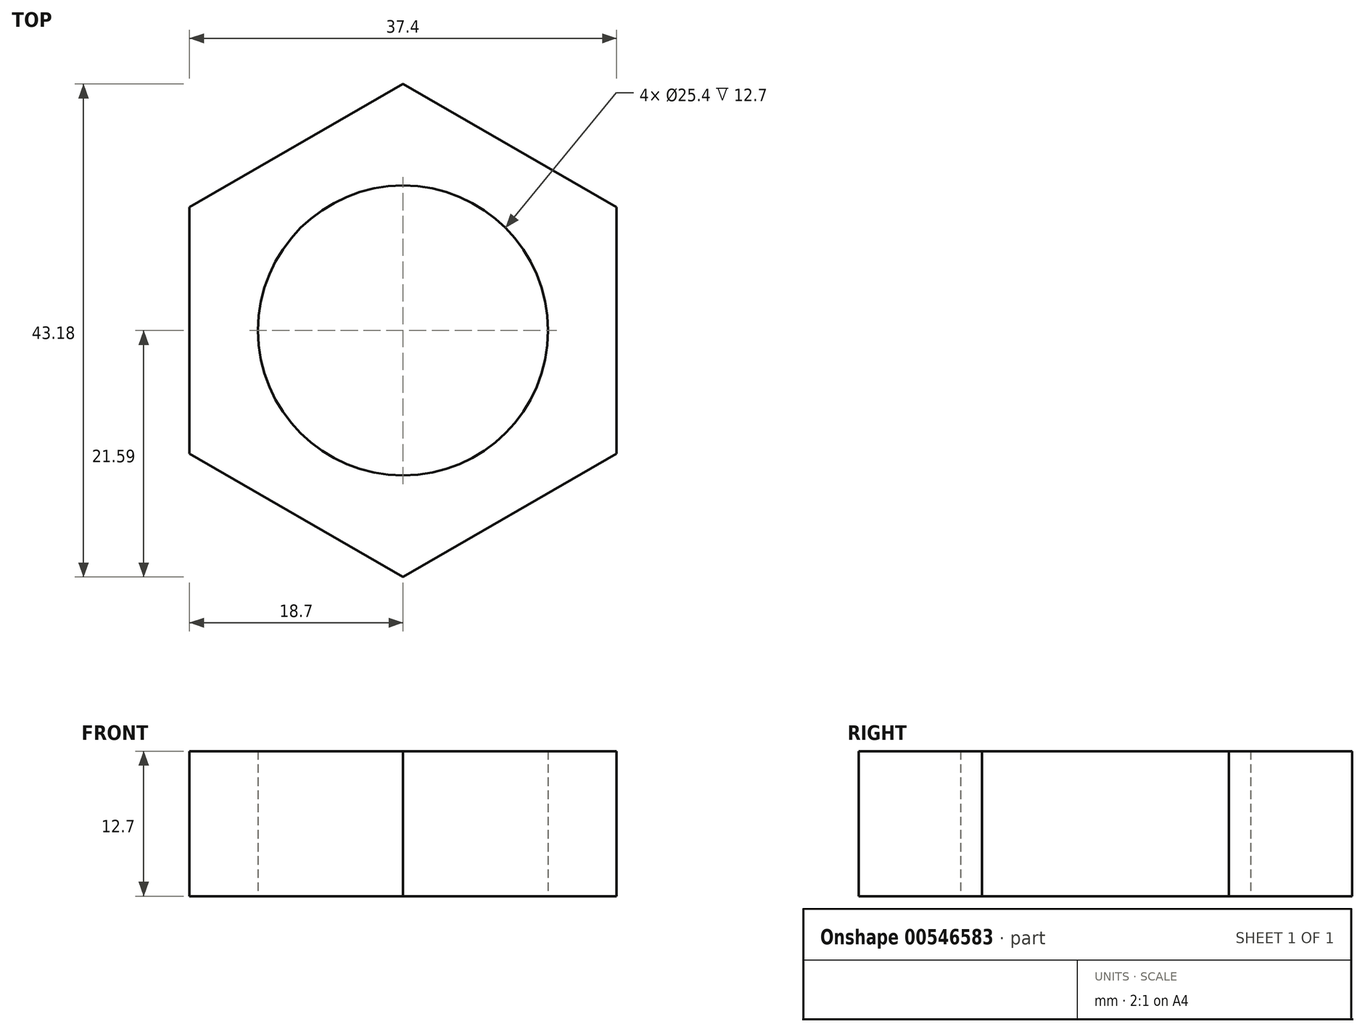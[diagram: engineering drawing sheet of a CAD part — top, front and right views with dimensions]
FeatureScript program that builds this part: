
annotation { "Feature Type Name" : "Feature", "Feature Type Description" : "" }
export const myFeature = defineFeature(function(context is Context, id is Id, definition is map)
    precondition{}
    {
        {
            var Q0;
            Q0=qCreatedBy(makeId("Top.planeOp"),FACE);
            var sketch = newSketch(context, id + "F0", { "sketchPlane" : qUnion([Q0])});
            skCircle(sketch, "E0", {"center": v(0, 0) * mm, "radius": 12.7 * mm});
            skCircle(sketch, "E1.cCircle", {"center": v(0, 0) * mm, "radius": 18.7 * mm, "construction": true});
            skLineSegment(sketch, "E1.0", {"start": v(18.7, 10.8) * mm, "end": v(18.7, -10.8) * mm});
            skLineSegment(sketch, "E1.1", {"start": v(18.7, -10.8) * mm, "end": v(0, -21.6) * mm});
            skLineSegment(sketch, "E1.2", {"start": v(0, -21.6) * mm, "end": v(-18.7, -10.8) * mm});
            skLineSegment(sketch, "E1.3", {"start": v(-18.7, -10.8) * mm, "end": v(-18.7, 10.8) * mm});
            skLineSegment(sketch, "E1.4", {"start": v(-18.7, 10.8) * mm, "end": v(0, 21.6) * mm});
            skLineSegment(sketch, "E1.5", {"start": v(0, 21.6) * mm, "end": v(18.7, 10.8) * mm});
            skPoint(sketch, "E1.0.midPoint", {"position": v(18.7, 0) * mm});
            skSolve(sketch);
        }
        {
            var Q0;
            Q0 = qSketchRegion(id + "F0", true);
            extrude(context, id + "F1", {"entities" : qUnion([Q0]), "depth" : 12.7 * mm, "offsetDistance" : 25.4 * mm});
        }
    });
